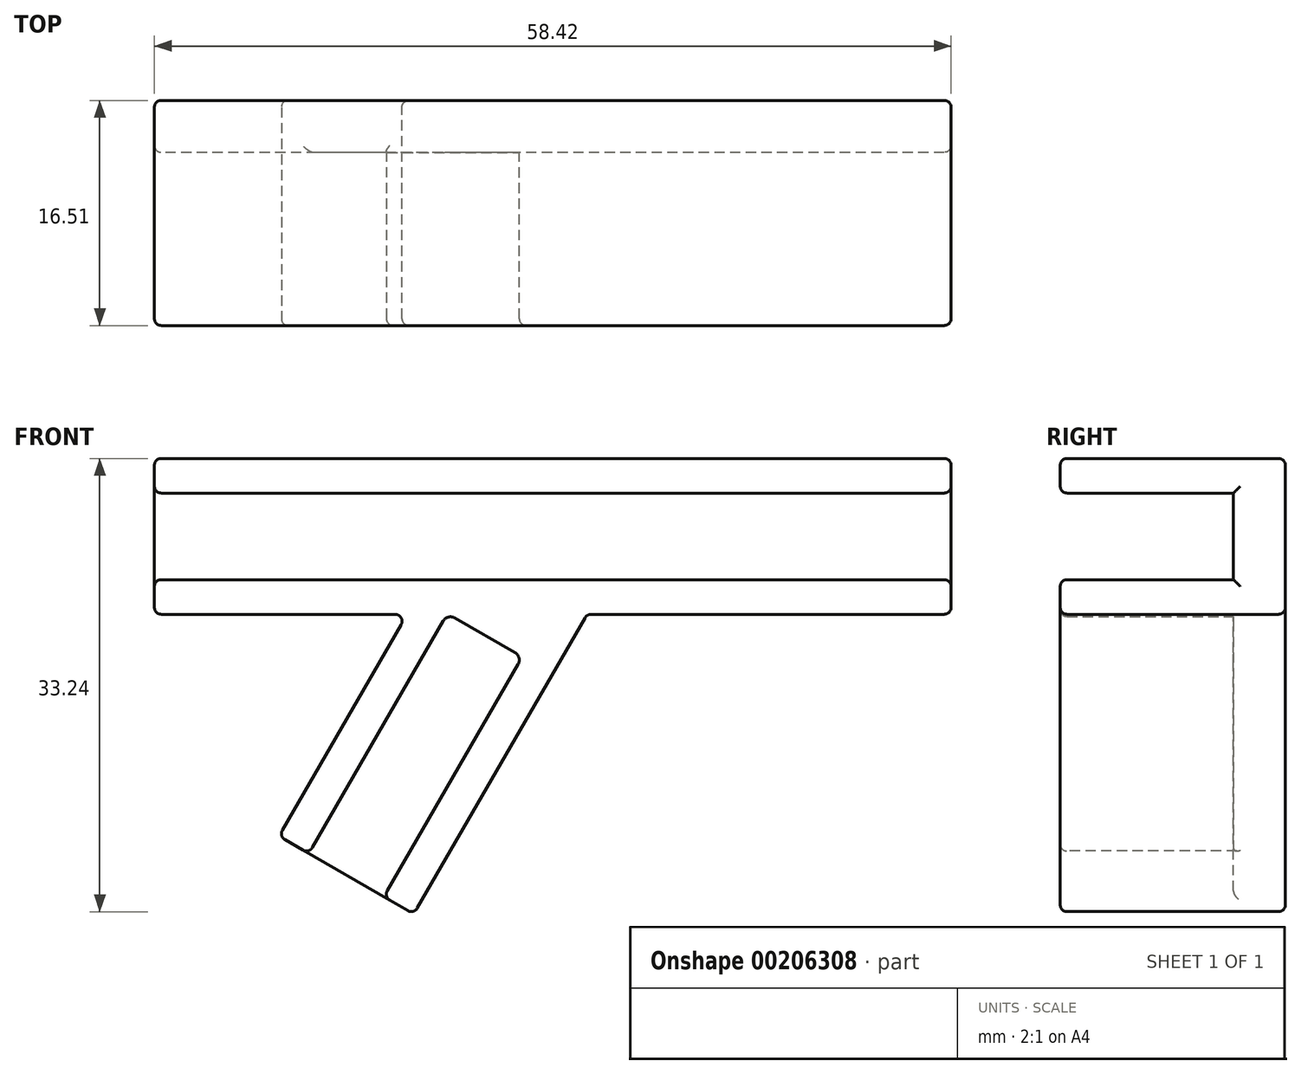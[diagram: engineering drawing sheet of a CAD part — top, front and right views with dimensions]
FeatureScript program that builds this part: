
annotation { "Feature Type Name" : "Feature", "Feature Type Description" : "" }
export const myFeature = defineFeature(function(context is Context, id is Id, definition is map)
    precondition{}
    {
        {
            var Q0;
            Q0=qCreatedBy(makeId("Front.planeOp"),FACE);
            var sketch = newSketch(context, id + "F0", { "sketchPlane" : qUnion([Q0])});
            skLineSegment(sketch, "E0.1", {"start": v(29.21, 3.18) * mm, "end": v(-29.2, 3.17) * mm});
            skLineSegment(sketch, "E0.4", {"start": v(-29.2, -3.17) * mm, "end": v(29.21, -3.18) * mm});
            skLineSegment(sketch, "E1", {"start": v(-29.2, 5.71) * mm, "end": v(29.21, 5.71) * mm});
            skLineSegment(sketch, "E2", {"start": v(29.21, -5.72) * mm, "end": v(2.52, -5.72) * mm});
            skLineSegment(sketch, "E3", {"start": v(29.21, 3.18) * mm, "end": v(29.21, 5.71) * mm});
            skLineSegment(sketch, "E4", {"start": v(29.21, -5.72) * mm, "end": v(29.21, -3.18) * mm});
            skLineSegment(sketch, "E5.1", {"start": v(-12.38, -26.44) * mm, "end": v(-2.54, -9.4) * mm});
            skLineSegment(sketch, "E5.4", {"start": v(-8.04, -6.22) * mm, "end": v(-17.88, -23.27) * mm});
            skLineSegment(sketch, "E6", {"start": v(2.52, -5.72) * mm, "end": v(-10.18, -27.71) * mm});
            skLineSegment(sketch, "E7", {"start": v(-20.08, -22) * mm, "end": v(-10.68, -5.72) * mm});
            skLineSegment(sketch, "E8", {"start": v(-12.38, -26.44) * mm, "end": v(-10.18, -27.71) * mm});
            skLineSegment(sketch, "E9", {"start": v(-20.08, -22) * mm, "end": v(-17.88, -23.27) * mm});
            skLineSegment(sketch, "E10", {"start": v(2.52, -5.72) * mm, "end": v(-7.38, 0) * mm, "construction": true});
            skArc(sketch, "E11.filletArc", {"start": v(-2.54, -9.4) * mm, "mid": v(-2.48, -8.91) * mm, "end": v(-2.77, -8.53) * mm});
            skArc(sketch, "E12.filletArc", {"start": v(-7.17, -5.99) * mm, "mid": v(-7.66, -5.92) * mm, "end": v(-8.04, -6.22) * mm});
            skPoint(sketch, "E13", {"position": v(-2.43, -2.86) * mm});
            skLineSegment(sketch, "E14", {"start": v(3.81, 3.17) * mm, "end": v(3.81, -3.17) * mm, "construction": true});
            skPoint(sketch, "E15", {"position": v(3.81, 0) * mm});
            skLineSegment(sketch, "E16", {"start": v(-29.2, 5.71) * mm, "end": v(-29.2, 3.18) * mm});
            skLineSegment(sketch, "E17", {"start": v(-29.2, -5.72) * mm, "end": v(-29.2, -3.18) * mm});
            skLineSegment(sketch, "E18", {"start": v(-29.2, -5.72) * mm, "end": v(-10.68, -5.72) * mm});
            skLineSegment(sketch, "E19", {"start": v(-2.77, -8.53) * mm, "end": v(-7.17, -5.99) * mm});
            skLineSegment(sketch, "E20", {"start": v(29.21, 3.18) * mm, "end": v(29.21, -3.18) * mm});
            skLineSegment(sketch, "E21", {"start": v(-29.2, 3.17) * mm, "end": v(-29.2, -3.17) * mm});
            skLineSegment(sketch, "E22", {"start": v(-12.38, -26.44) * mm, "end": v(-17.88, -23.27) * mm});
            skSolve(sketch);
        }
        {
            var Q0;
            Q0=makeQuery(id+"F0.imprint","IMPRINT",FACE,{"disambiguationData":[TD([[makeQuery(id+"F0.imprint","IMPRINT",EDGE,{"derivedFrom":sQuery(id+"F0.wireOp",EDGE,"E0.4")}),-1.0]])]});
            var Q1;
            Q1=makeQuery(id+"F0.imprint","IMPRINT",FACE,{"disambiguationData":[TD([[makeQuery(id+"F0.imprint","IMPRINT",EDGE,{"derivedFrom":sQuery(id+"F0.wireOp",EDGE,"E0.1")}),-1.0]])]});
            extrude(context, id + "F1", {"entities" : qUnion([Q0, Q1]), "depth" : 12.7 * mm});
        }
        {
            var Q0;
            Q0=makeQuery(id+"F0.imprint","IMPRINT",FACE,{"disambiguationData":[TD([[makeQuery(id+"F0.imprint","IMPRINT",EDGE,{"derivedFrom":sQuery(id+"F0.wireOp",EDGE,"E0.1")}),-1.0]])]});
            var Q1;
            Q1=makeQuery(id+"F0.imprint","IMPRINT",FACE,{"disambiguationData":[TD([[makeQuery(id+"F0.imprint","IMPRINT",EDGE,{"derivedFrom":sQuery(id+"F0.wireOp",EDGE,"E0.1")}),1.0]])]});
            var Q2;
            Q2=makeQuery(id+"F0.imprint","IMPRINT",FACE,{"disambiguationData":[TD([[makeQuery(id+"F0.imprint","IMPRINT",EDGE,{"derivedFrom":sQuery(id+"F0.wireOp",EDGE,"E5.1")}),1.0]])]});
            var Q3;
            Q3=makeQuery(id+"F0.imprint","IMPRINT",FACE,{"disambiguationData":[TD([[makeQuery(id+"F0.imprint","IMPRINT",EDGE,{"derivedFrom":sQuery(id+"F0.wireOp",EDGE,"E0.4")}),-1.0]])]});
            extrude(context, id + "F2", {"entities" : qUnion([Q0, Q1, Q2, Q3]), "oppositeDirection" : true, "depth" : 3.8 * mm});
        }
        {
            var Q0;
            Q0=makeQuery(id+"F1.opExtrude","SWEPT_BODY",BODY,{"disambiguationData":[OSD([sQuery(id+"F0.wireOp",EDGE,"E0.1"),sQuery(id+"F0.wireOp",EDGE,"E1"),sQuery(id+"F0.wireOp",EDGE,"E3"),sQuery(id+"F0.wireOp",EDGE,"E16")])]});
            var Q1;
            Q1=makeQuery(id+"F1.opExtrude","SWEPT_BODY",BODY,{"disambiguationData":[OSD([sQuery(id+"F0.wireOp",EDGE,"E0.4"),sQuery(id+"F0.wireOp",EDGE,"E2"),sQuery(id+"F0.wireOp",EDGE,"E4"),sQuery(id+"F0.wireOp",EDGE,"E5.1"),sQuery(id+"F0.wireOp",EDGE,"E5.4"),sQuery(id+"F0.wireOp",EDGE,"E6"),sQuery(id+"F0.wireOp",EDGE,"E7"),sQuery(id+"F0.wireOp",EDGE,"E8"),sQuery(id+"F0.wireOp",EDGE,"E9"),sQuery(id+"F0.wireOp",EDGE,"E11.filletArc"),sQuery(id+"F0.wireOp",EDGE,"E12.filletArc"),sQuery(id+"F0.wireOp",EDGE,"E17"),sQuery(id+"F0.wireOp",EDGE,"E18"),sQuery(id+"F0.wireOp",EDGE,"E19")])]});
            var Q2;
            Q2=makeQuery(id+"F2.opExtrude","SWEPT_BODY",BODY,{"disambiguationData":[OSD([sQuery(id+"F0.wireOp",EDGE,"E1"),sQuery(id+"F0.wireOp",EDGE,"E2"),sQuery(id+"F0.wireOp",EDGE,"E3"),sQuery(id+"F0.wireOp",EDGE,"E4"),sQuery(id+"F0.wireOp",EDGE,"E6"),sQuery(id+"F0.wireOp",EDGE,"E7"),sQuery(id+"F0.wireOp",EDGE,"E8"),sQuery(id+"F0.wireOp",EDGE,"E9"),sQuery(id+"F0.wireOp",EDGE,"E16"),sQuery(id+"F0.wireOp",EDGE,"E17"),sQuery(id+"F0.wireOp",EDGE,"E18"),sQuery(id+"F0.wireOp",EDGE,"E20"),sQuery(id+"F0.wireOp",EDGE,"E21"),sQuery(id+"F0.wireOp",EDGE,"E22")])]});
            booleanBodies(context, id + "F3", {"operationType" : BooleanOperationType.UNION, "tools" : qUnion([Q0, Q1, Q2])});
        }
        {
            var Q0;
            Q0=makeQuery(id+"F2.opExtrude","CAP_FACE",FACE,{"disambiguationData":[OSD([sQuery(id+"F0.wireOp",EDGE,"E1"),sQuery(id+"F0.wireOp",EDGE,"E2"),sQuery(id+"F0.wireOp",EDGE,"E3"),sQuery(id+"F0.wireOp",EDGE,"E4"),sQuery(id+"F0.wireOp",EDGE,"E6"),sQuery(id+"F0.wireOp",EDGE,"E7"),sQuery(id+"F0.wireOp",EDGE,"E8"),sQuery(id+"F0.wireOp",EDGE,"E9"),sQuery(id+"F0.wireOp",EDGE,"E16"),sQuery(id+"F0.wireOp",EDGE,"E17"),sQuery(id+"F0.wireOp",EDGE,"E18"),sQuery(id+"F0.wireOp",EDGE,"E20"),sQuery(id+"F0.wireOp",EDGE,"E21"),sQuery(id+"F0.wireOp",EDGE,"E22")])],"isStart":false});
            var Q1;
            {var subQ0=sQuery(id+"F0.wireOp",EDGE,"E6");Q1=makeQuery(id+"F3.opBoolean","MERGE",FACE,{"derivedFrom":[makeQuery(id+"F1.opExtrude","SWEPT_FACE",FACE,{"disambiguationData":[OSD([subQ0])]}),makeQuery(id+"F2.opExtrude","SWEPT_FACE",FACE,{"disambiguationData":[OSD([subQ0])]})]});}
            var Q2;
            {var subQ0=sQuery(id+"F0.wireOp",EDGE,"E2");Q2=makeQuery(id+"F3.opBoolean","MERGE",FACE,{"derivedFrom":[makeQuery(id+"F1.opExtrude","SWEPT_FACE",FACE,{"disambiguationData":[OSD([subQ0])]}),makeQuery(id+"F2.opExtrude","SWEPT_FACE",FACE,{"disambiguationData":[OSD([subQ0])]})]});}
            var Q3;
            {var subQ0=sQuery(id+"F0.wireOp",EDGE,"E4");var subQ1=sQuery(id+"F0.wireOp",EDGE,"E3");Q3=makeQuery(id+"F3.opBoolean","MERGE",FACE,{"derivedFrom":[makeQuery(id+"F1.opExtrude","SWEPT_FACE",FACE,{"disambiguationData":[OSD([subQ1])]}),makeQuery(id+"F1.opExtrude","SWEPT_FACE",FACE,{"disambiguationData":[OSD([subQ0])]}),makeQuery(id+"F2.opExtrude","SWEPT_FACE",FACE,{"disambiguationData":[OSD([subQ1,subQ0,sQuery(id+"F0.wireOp",EDGE,"E20")])]})]});}
            var Q4;
            {var subQ0=sQuery(id+"F0.wireOp",EDGE,"E1");Q4=makeQuery(id+"F3.opBoolean","MERGE",FACE,{"derivedFrom":[makeQuery(id+"F1.opExtrude","SWEPT_FACE",FACE,{"disambiguationData":[OSD([subQ0])]}),makeQuery(id+"F2.opExtrude","SWEPT_FACE",FACE,{"disambiguationData":[OSD([subQ0])]})]});}
            var Q5;
            Q5=makeQuery(id+"F1.opExtrude","CAP_FACE",FACE,{"disambiguationData":[OSD([sQuery(id+"F0.wireOp",EDGE,"E0.1"),sQuery(id+"F0.wireOp",EDGE,"E1"),sQuery(id+"F0.wireOp",EDGE,"E3"),sQuery(id+"F0.wireOp",EDGE,"E16")])],"isStart":false});
            var Q6;
            Q6=makeQuery(id+"F1.opExtrude","CAP_FACE",FACE,{"disambiguationData":[OSD([sQuery(id+"F0.wireOp",EDGE,"E0.4"),sQuery(id+"F0.wireOp",EDGE,"E2"),sQuery(id+"F0.wireOp",EDGE,"E4"),sQuery(id+"F0.wireOp",EDGE,"E5.1"),sQuery(id+"F0.wireOp",EDGE,"E5.4"),sQuery(id+"F0.wireOp",EDGE,"E6"),sQuery(id+"F0.wireOp",EDGE,"E7"),sQuery(id+"F0.wireOp",EDGE,"E8"),sQuery(id+"F0.wireOp",EDGE,"E9"),sQuery(id+"F0.wireOp",EDGE,"E11.filletArc"),sQuery(id+"F0.wireOp",EDGE,"E12.filletArc"),sQuery(id+"F0.wireOp",EDGE,"E17"),sQuery(id+"F0.wireOp",EDGE,"E18"),sQuery(id+"F0.wireOp",EDGE,"E19")])],"isStart":false});
            var Q7;
            {var subQ0=sQuery(id+"F0.wireOp",EDGE,"E17");var subQ1=sQuery(id+"F0.wireOp",EDGE,"E16");Q7=makeQuery(id+"F3.opBoolean","MERGE",FACE,{"derivedFrom":[makeQuery(id+"F1.opExtrude","SWEPT_FACE",FACE,{"disambiguationData":[OSD([subQ1])]}),makeQuery(id+"F1.opExtrude","SWEPT_FACE",FACE,{"disambiguationData":[OSD([subQ0])]}),makeQuery(id+"F2.opExtrude","SWEPT_FACE",FACE,{"disambiguationData":[OSD([subQ1,subQ0,sQuery(id+"F0.wireOp",EDGE,"E21")])]})]});}
            var Q8;
            {var subQ0=sQuery(id+"F0.wireOp",EDGE,"E18");Q8=makeQuery(id+"F3.opBoolean","MERGE",FACE,{"derivedFrom":[makeQuery(id+"F1.opExtrude","SWEPT_FACE",FACE,{"disambiguationData":[OSD([subQ0])]}),makeQuery(id+"F2.opExtrude","SWEPT_FACE",FACE,{"disambiguationData":[OSD([subQ0])]})]});}
            var Q9;
            {var subQ0=sQuery(id+"F0.wireOp",EDGE,"E9");var subQ1=sQuery(id+"F0.wireOp",EDGE,"E8");Q9=makeQuery(id+"F3.opBoolean","MERGE",FACE,{"derivedFrom":[makeQuery(id+"F1.opExtrude","SWEPT_FACE",FACE,{"disambiguationData":[OSD([subQ1])]}),makeQuery(id+"F1.opExtrude","SWEPT_FACE",FACE,{"disambiguationData":[OSD([subQ0])]}),makeQuery(id+"F2.opExtrude","SWEPT_FACE",FACE,{"disambiguationData":[OSD([subQ1,subQ0,sQuery(id+"F0.wireOp",EDGE,"E22")])]})]});}
            fillet(context, id + "F4", {"entities" : qUnion([Q0, Q1, Q2, Q3, Q4, Q5, Q6, Q7, Q8, Q9]), "radius" : 0.5 * mm, "tangentPropagation" : true, "allowEdgeOverflow" : false});
        }
    });
